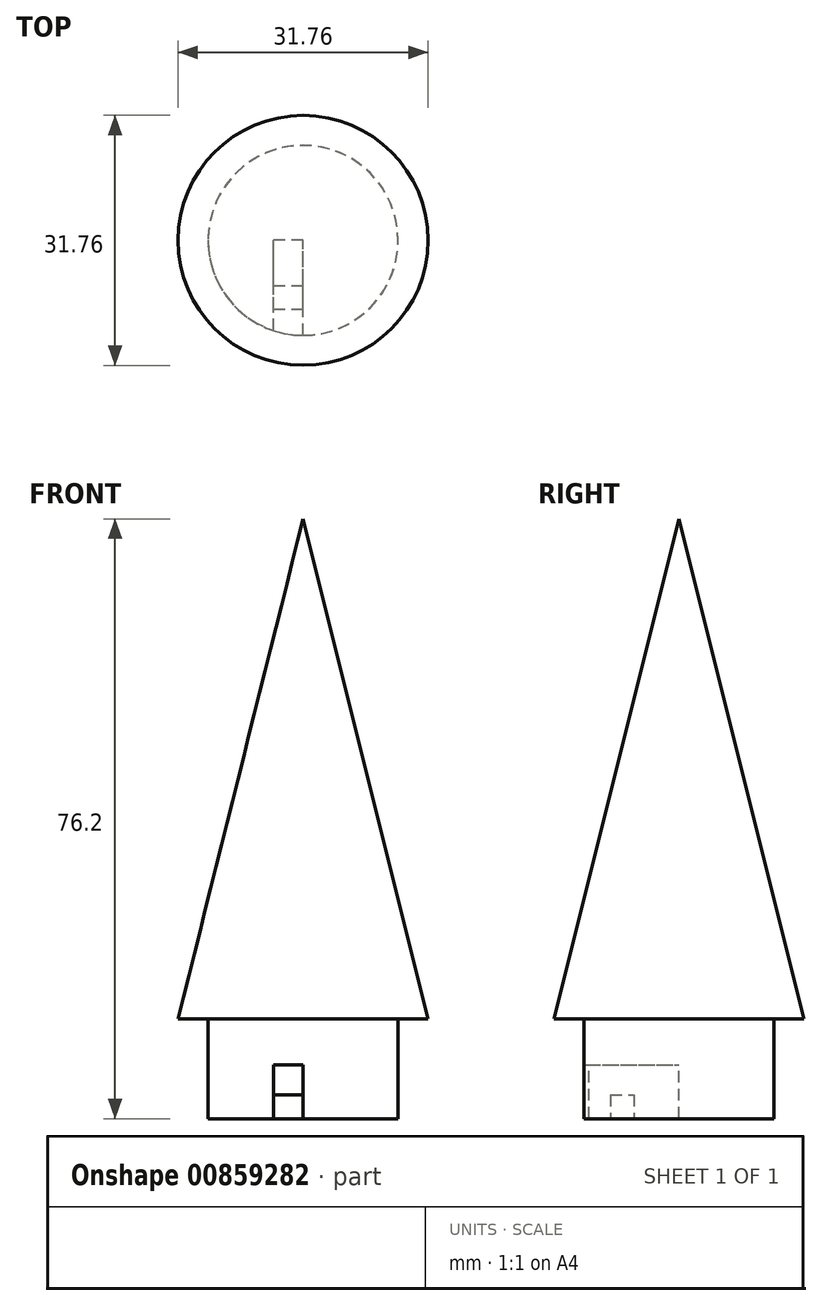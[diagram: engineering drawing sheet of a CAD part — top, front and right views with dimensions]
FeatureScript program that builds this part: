
annotation { "Feature Type Name" : "Feature", "Feature Type Description" : "" }
export const myFeature = defineFeature(function(context is Context, id is Id, definition is map)
    precondition{}
    {
        {
            var Q0;
            Q0=qCreatedBy(makeId("Front.planeOp"),FACE);
            var sketch = newSketch(context, id + "F0", { "sketchPlane" : qUnion([Q0])});
            skLineSegment(sketch, "E0", {"start": v(0, 0) * mm, "end": v(0, 63.5) * mm});
            skLineSegment(sketch, "E1", {"start": v(0, 63.5) * mm, "end": v(15.88, 0) * mm});
            skLineSegment(sketch, "E2", {"start": v(15.87, 0) * mm, "end": v(0, 0) * mm});
            skSolve(sketch);
        }
        {
            var Q0;
            Q0=makeQuery(id+"F0.imprint","IMPRINT",FACE,{"disambiguationData":[TD([[makeQuery(id+"F0.imprint","IMPRINT",EDGE,{"derivedFrom":sQuery(id+"F0.wireOp",EDGE,"E0")}),-1.0]])]});
            var Q1;
            Q1=sQuery(id+"F0.wireOp",EDGE,"E0");
            revolve(context, id + "F1", {"surfaceOperationType" : NewSurfaceOperationType.NEW, "entities" : qUnion([Q0]), "axis" : qUnion([Q1]), "revolveType" : RevolveType.FULL, "oppositeDirection" : true});
        }
        {
            var Q0;
            Q0=makeQuery(id+"F1.opRevolve","SWEPT_FACE",FACE,{"disambiguationData":[OSD([sQuery(id+"F0.wireOp",EDGE,"E2")])]});
            var sketch = newSketch(context, id + "F2", { "sketchPlane" : qUnion([Q0])});
            skCircle(sketch, "E3", {"center": v(0, 0) * mm, "radius": 12.06 * mm});
            skSolve(sketch);
        }
        {
            var Q0;
            Q0 = qSketchRegion(id + "F2", true);
            extrude(context, id + "F3", {"entities" : qUnion([Q0]), "operationType" : NewBodyOperationType.ADD, "depth" : 12.7 * mm, "offsetDistance" : 25.4 * mm});
        }
        {
            var Q0;
            Q0=qCreatedBy(makeId("Front.planeOp"),FACE);
            var sketch = newSketch(context, id + "F4", { "sketchPlane" : qUnion([Q0])});
            skLineSegment(sketch, "E4.bottom", {"start": v(0, -13.92) * mm, "end": v(-3.77, -13.92) * mm});
            skLineSegment(sketch, "E4.top", {"start": v(0, -5.85) * mm, "end": v(-3.77, -5.85) * mm});
            skLineSegment(sketch, "E4.left", {"start": v(0, -13.92) * mm, "end": v(0, -5.85) * mm});
            skLineSegment(sketch, "E4.right", {"start": v(-3.77, -13.92) * mm, "end": v(-3.77, -5.85) * mm});
            skSolve(sketch);
        }
        {
            var Q0;
            Q0 = qSketchRegion(id + "F4", true);
            extrude(context, id + "F5", {"entities" : qUnion([Q0]), "operationType" : NewBodyOperationType.REMOVE, "depth" : 12.7 * mm, "offsetDistance" : 25.4 * mm});
        }
        {
            var Q0;
            Q0=makeQuery(id+"F3.opExtrude","CAP_FACE",FACE,{"disambiguationData":[OSD([sQuery(id+"F2.wireOp",EDGE,"E3")])],"isStart":false});
            var sketch = newSketch(context, id + "F6", { "sketchPlane" : qUnion([Q0])});
            skLineSegment(sketch, "E5.bottom", {"start": v(-3.77, 5.73) * mm, "end": v(0, 5.73) * mm});
            skLineSegment(sketch, "E5.top", {"start": v(-3.77, 8.74) * mm, "end": v(0, 8.74) * mm});
            skLineSegment(sketch, "E5.left", {"start": v(-3.77, 5.73) * mm, "end": v(-3.77, 8.74) * mm});
            skLineSegment(sketch, "E5.right", {"start": v(0, 5.73) * mm, "end": v(0, 8.74) * mm});
            skSolve(sketch);
        }
        {
            var Q0;
            Q0 = qSketchRegion(id + "F6", true);
            extrude(context, id + "F7", {"entities" : qUnion([Q0]), "operationType" : NewBodyOperationType.ADD, "oppositeDirection" : true, "depth" : 3.05 * mm, "offsetDistance" : 25.4 * mm});
        }
    });
